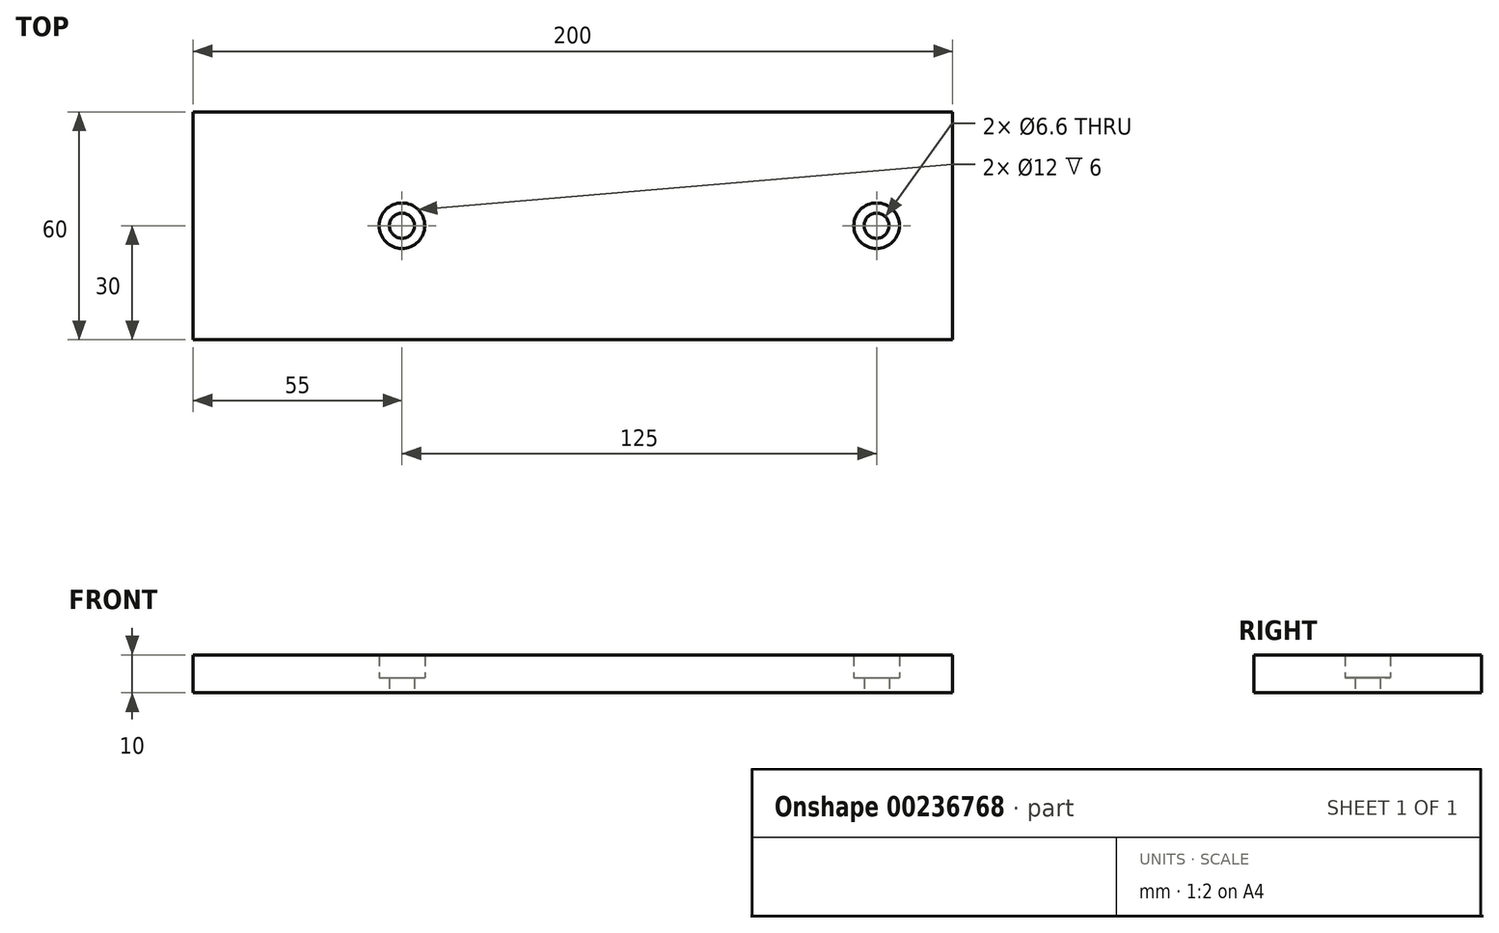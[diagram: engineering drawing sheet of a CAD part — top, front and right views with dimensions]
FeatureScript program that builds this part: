
annotation { "Feature Type Name" : "Feature", "Feature Type Description" : "" }
export const myFeature = defineFeature(function(context is Context, id is Id, definition is map)
    precondition{}
    {
        {
            var Q0;
            Q0=qCreatedBy(makeId("Top.planeOp"),FACE);
            var sketch = newSketch(context, id + "F0", { "sketchPlane" : qUnion([Q0])});
            skLineSegment(sketch, "E0.bottom", {"start": v(0, 0) * mm, "end": v(200, 0) * mm});
            skLineSegment(sketch, "E0.top", {"start": v(0, 60) * mm, "end": v(200, 60) * mm});
            skLineSegment(sketch, "E0.left", {"start": v(0, 0) * mm, "end": v(0, 60) * mm});
            skLineSegment(sketch, "E0.right", {"start": v(200, 0) * mm, "end": v(200, 60) * mm});
            skSolve(sketch);
        }
        {
            var Q0;
            Q0=makeQuery(id+"F0.imprint","IMPRINT",FACE,{"disambiguationData":[TD([[makeQuery(id+"F0.imprint","IMPRINT",EDGE,{"derivedFrom":sQuery(id+"F0.wireOp",EDGE,"E0.bottom")}),1.0]])]});
            extrude(context, id + "F1", {"entities" : qUnion([Q0]), "depth" : 10 * mm, "offsetDistance" : 25 * mm});
        }
        {
            var Q0;
            Q0=makeQuery(id+"F1.opExtrude","CAP_FACE",FACE,{"disambiguationData":[OSD([sQuery(id+"F0.wireOp",EDGE,"E0.bottom"),sQuery(id+"F0.wireOp",EDGE,"E0.top"),sQuery(id+"F0.wireOp",EDGE,"E0.left"),sQuery(id+"F0.wireOp",EDGE,"E0.right")])],"isStart":false});
            var sketch = newSketch(context, id + "F2", { "sketchPlane" : qUnion([Q0])});
            skPoint(sketch, "E1", {"position": v(55, 30) * mm});
            skPoint(sketch, "E1.positionSnap0", {"position": v(0, 30) * mm});
            skPoint(sketch, "E2", {"position": v(180, 30) * mm});
            skSolve(sketch);
        }
        {
            var Q0;
            Q0=sQuery(id+"F2.wireOp",VERTEX,"E2");
            var Q1;
            Q1=sQuery(id+"F2.wireOp",VERTEX,"E1");
            var Q2;
            Q2=makeQuery(id+"F1.opExtrude","SWEPT_BODY",BODY,{"disambiguationData":[OSD([sQuery(id+"F0.wireOp",EDGE,"E0.bottom"),sQuery(id+"F0.wireOp",EDGE,"E0.top"),sQuery(id+"F0.wireOp",EDGE,"E0.left"),sQuery(id+"F0.wireOp",EDGE,"E0.right")])]});
            hole(context, id + "F3", {"style" : HoleStyle.C_BORE, "endStyle" : HoleEndStyle.THROUGH, "holeDiameter" : 6.6 * mm, "cBoreDiameter" : 12 * mm, "cBoreDepth" : 6 * mm, "majorDiameter" : 5 * mm, "isTappedThrough" : true, "tappedDepth" : 31.25 * mm, "tapClearance" : 3, "startFromSketch" : true, "locations" : qUnion([Q0, Q1]), "scope" : qUnion([Q2])});
        }
    });
